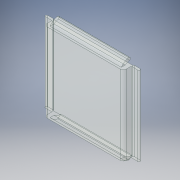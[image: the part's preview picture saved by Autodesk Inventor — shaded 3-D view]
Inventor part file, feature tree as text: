
AUTODESK INVENTOR PART (.ipt)
format: ipt  version: 2019 (Build 230136000, 136)  size: 159,232 bytes
history: native  units: mm
features: sketch x4, fillet x3, extrude x2, sweep x1, mirror x1, plane x1, projected_geometry x1
ambient origin geometry x8: Origin, YZ Plane, XZ Plane, XY Plane, X Axis, Y Axis, Z Axis, Center Point
bodies: Solid1 (feature_tree)
feature tree (13):
  extrude  "Extrusion1"  Depth=100.0mm
  sweep  "Sweep1"
  mirror  "Mirror1"
  fillet  "Fillet2"  Radius=5.0mm
  plane  "Work Plane1"
  extrude  "Extrusion3"  Depth=4.0mm
  fillet  "Fillet3"  [1 undecoded]
  fillet  "Fillet4"  Radius=10.0mm
  sketch  "Sketch1"  dims[d0=100.0mm d1=100.0mm]
  sketch  "Sketch2"  dims[d2=12.0mm d3=0.0mm d4=90.0mm d5=5.0mm]
  projected_geometry  "Projected Loop1"
  sketch  "Sketch3"  dims[d8=0.0mm d9=0.0mm d11=4.0mm d16=-10.0mm d17=10.0mm]
  sketch  "Sketch5"  dims[d18=100.0mm d19=3.0mm d20=0.0mm d21=1.5mm d24=1.5mm]
note: 1 required parameter value undecoded (feature->parameter linkage not recoverable at this tier; creation-order binding heuristic only, values carry confidence <= 0.55)
